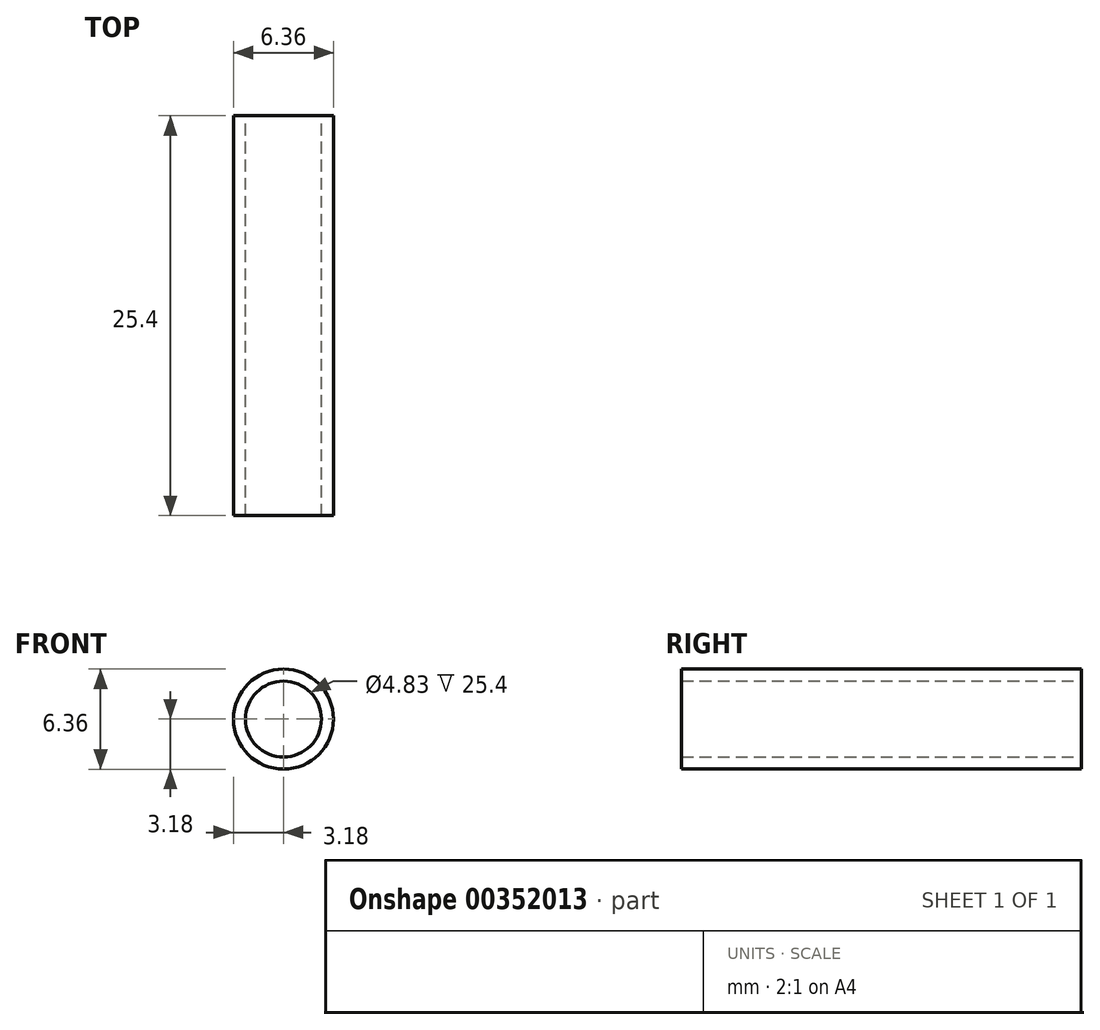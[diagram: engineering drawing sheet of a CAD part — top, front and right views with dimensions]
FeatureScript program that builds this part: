
annotation { "Feature Type Name" : "Feature", "Feature Type Description" : "" }
export const myFeature = defineFeature(function(context is Context, id is Id, definition is map)
    precondition{}
    {
        {
            var Q0;
            Q0=qCreatedBy(makeId("Front.planeOp"),FACE);
            var sketch = newSketch(context, id + "F0", { "sketchPlane" : qUnion([Q0])});
            skCircle(sketch, "E0", {"center": v(0, 0) * mm, "radius": 2.41 * mm});
            skCircle(sketch, "E1", {"center": v(0, 0) * mm, "radius": 3.18 * mm});
            skSolve(sketch);
        }
        {
            var Q0;
            Q0=makeQuery(id+"F0.imprint","IMPRINT",FACE,{"disambiguationData":[TD([[makeQuery(id+"F0.imprint","IMPRINT",EDGE,{"derivedFrom":sQuery(id+"F0.wireOp",EDGE,"E0")}),-1.0]])]});
            extrude(context, id + "F1", {"entities" : qUnion([Q0]), "depth" : 25.4 * mm});
        }
    });
